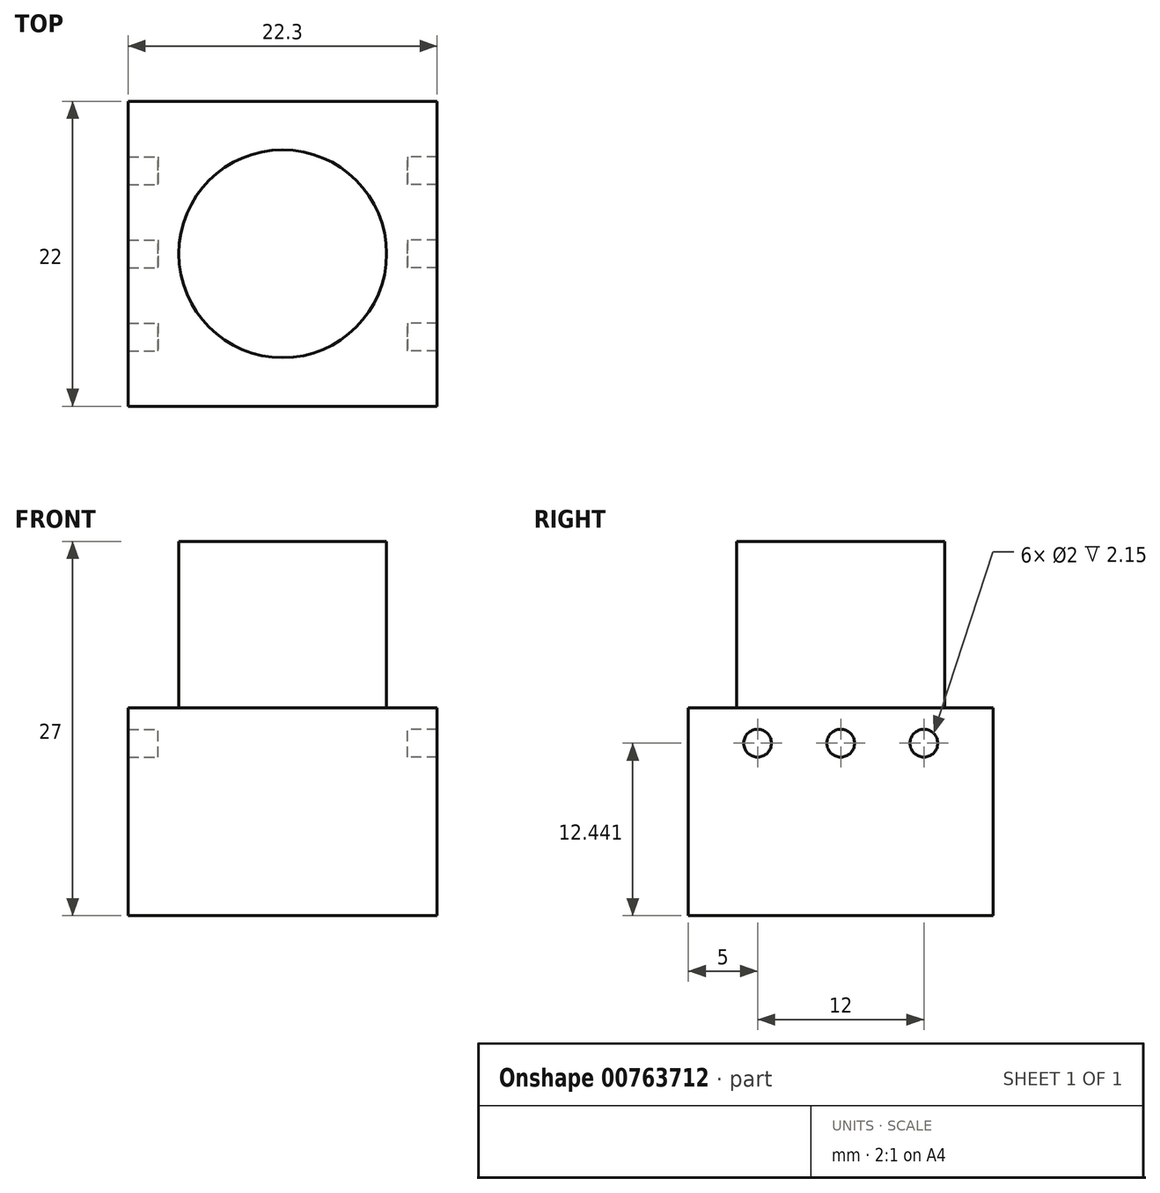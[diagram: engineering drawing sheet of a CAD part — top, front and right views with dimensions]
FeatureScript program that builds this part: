
annotation { "Feature Type Name" : "Feature", "Feature Type Description" : "" }
export const myFeature = defineFeature(function(context is Context, id is Id, definition is map)
    precondition{}
    {
        {
            var Q0;
            Q0=qCreatedBy(makeId("Top.planeOp"),FACE);
            var sketch = newSketch(context, id + "F0", { "sketchPlane" : qUnion([Q0])});
            skLineSegment(sketch, "E0.bottom", {"start": v(11.15, 11) * mm, "end": v(-11.15, 11) * mm});
            skLineSegment(sketch, "E0.top", {"start": v(11.15, -11) * mm, "end": v(-11.15, -11) * mm});
            skLineSegment(sketch, "E0.left", {"start": v(11.15, 11) * mm, "end": v(11.15, -11) * mm});
            skLineSegment(sketch, "E0.right", {"start": v(-11.15, 11) * mm, "end": v(-11.15, -11) * mm});
            skPoint(sketch, "E0.middle", {"position": v(0, 0) * mm});
            skSolve(sketch);
        }
        {
            var Q0;
            Q0 = qSketchRegion(id + "F0", true);
            extrude(context, id + "F1", {"entities" : qUnion([Q0]), "depth" : 15 * mm, "offsetDistance" : 25 * mm});
        }
        {
            var Q0;
            Q0=qCreatedBy(makeId("Top.planeOp"),FACE);
            var sketch = newSketch(context, id + "F2", { "sketchPlane" : qUnion([Q0])});
            skCircle(sketch, "E1", {"center": v(0, 0) * mm, "radius": 7.5 * mm});
            skSolve(sketch);
        }
        {
            var Q0;
            Q0 = qSketchRegion(id + "F2", true);
            extrude(context, id + "F3", {"entities" : qUnion([Q0]), "operationType" : NewBodyOperationType.ADD, "depth" : 27 * mm, "offsetDistance" : 25 * mm, "hasSecondDirection" : true, "secondDirectionOppositeDirection" : false, "secondDirectionDepth" : 15 * mm});
        }
        {
            var Q0;
            Q0=qCreatedBy(makeId("Right.planeOp"),FACE);
            var sketch = newSketch(context, id + "F4", { "sketchPlane" : qUnion([Q0])});
            skLineSegment(sketch, "E2", {"start": v(0, 12.44) * mm, "end": v(6, 12.44) * mm, "construction": true});
            skLineSegment(sketch, "E3", {"start": v(0, 12.44) * mm, "end": v(-6, 12.44) * mm, "construction": true});
            skCircle(sketch, "E4", {"center": v(6, 12.44) * mm, "radius": 1 * mm});
            skCircle(sketch, "E5", {"center": v(0, 12.44) * mm, "radius": 1 * mm});
            skCircle(sketch, "E6", {"center": v(-6, 12.44) * mm, "radius": 1 * mm});
            skSolve(sketch);
        }
        {
            var Q0;
            Q0 = qSketchRegion(id + "F4", true);
            extrude(context, id + "F5", {"entities" : qUnion([Q0]), "operationType" : NewBodyOperationType.REMOVE, "oppositeDirection" : true, "depth" : 12 * mm, "offsetDistance" : 25 * mm, "hasSecondDirection" : true, "secondDirectionOppositeDirection" : true, "secondDirectionDepth" : 9 * mm});
        }
        {
            var Q0;
            Q0 = qSketchRegion(id + "F4", true);
            extrude(context, id + "F6", {"entities" : qUnion([Q0]), "operationType" : NewBodyOperationType.REMOVE, "depth" : 13 * mm, "offsetDistance" : 25 * mm, "hasSecondDirection" : true, "secondDirectionOppositeDirection" : false, "secondDirectionDepth" : 9 * mm});
        }
    });
